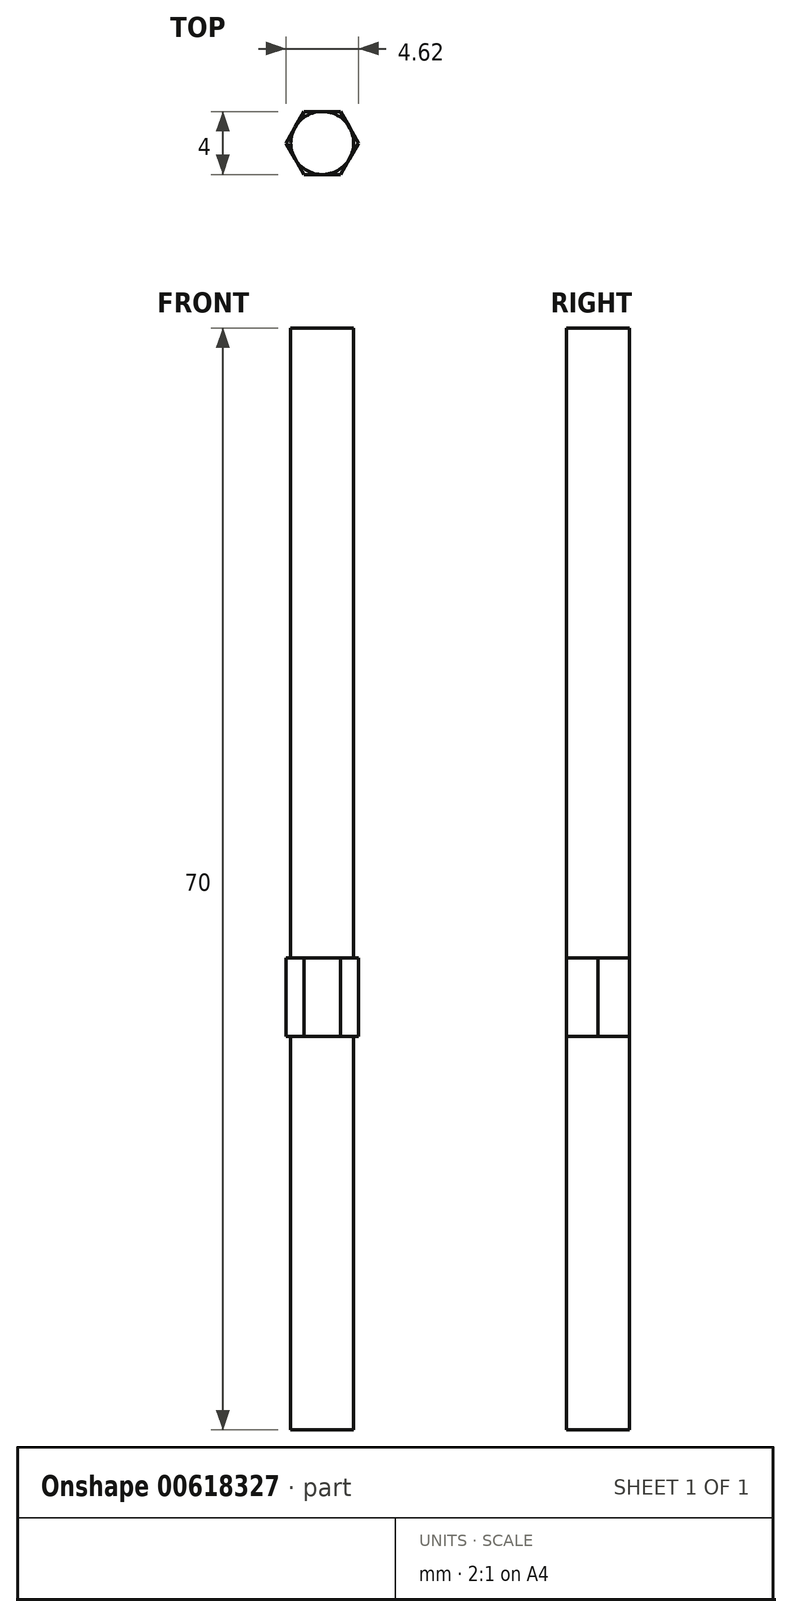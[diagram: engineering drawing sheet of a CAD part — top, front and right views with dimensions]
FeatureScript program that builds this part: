
annotation { "Feature Type Name" : "Feature", "Feature Type Description" : "" }
export const myFeature = defineFeature(function(context is Context, id is Id, definition is map)
    precondition{}
    {
        {
            var Q0;
            Q0=qCreatedBy(makeId("Top.planeOp"),FACE);
            var sketch = newSketch(context, id + "F0", { "sketchPlane" : qUnion([Q0])});
            skCircle(sketch, "E0", {"center": v(0, 0) * mm, "radius": 2 * mm});
            skSolve(sketch);
        }
        {
            var Q0;
            Q0=qSketchRegion(id+"F0",true);
            extrude(context, id + "F1", {"entities" : qUnion([Q0]), "depth" : 25 * mm, "offsetDistance" : 25 * mm});
        }
        {
            var Q0;
            Q0=makeQuery(id+"F1.opExtrude","CAP_FACE",FACE,{"disambiguationData":[OSD([sQuery(id+"F0.wireOp",EDGE,"E0")])],"isStart":false});
            var sketch = newSketch(context, id + "F2", { "sketchPlane" : qUnion([Q0])});
            skCircle(sketch, "E1.cCircle", {"center": v(0, 0) * mm, "radius": 2 * mm, "construction": true});
            skLineSegment(sketch, "E1.0", {"start": v(-1.15, 2) * mm, "end": v(1.15, 2) * mm});
            skLineSegment(sketch, "E1.1", {"start": v(1.15, 2) * mm, "end": v(2.3, 0) * mm});
            skLineSegment(sketch, "E1.2", {"start": v(2.3, 0) * mm, "end": v(1.15, -2) * mm});
            skLineSegment(sketch, "E1.3", {"start": v(1.15, -2) * mm, "end": v(-1.15, -2) * mm});
            skLineSegment(sketch, "E1.4", {"start": v(-1.15, -2) * mm, "end": v(-2.3, 0) * mm});
            skLineSegment(sketch, "E1.5", {"start": v(-2.3, 0) * mm, "end": v(-1.15, 2) * mm});
            skPoint(sketch, "E1.0.midPoint", {"position": v(0, 2) * mm});
            skSolve(sketch);
        }
        {
            var Q0;
            {var subQ0=sQuery(id+"F2.wireOp",EDGE,"E1.5");var subQ1=sQuery(id+"F2.wireOp",EDGE,"E1.0");var subQ2=makeQuery(id+"F2.imprint","INTERSECT",VERTEX,{"derivedFrom":[subQ1,subQ0]});Q0=makeQuery(id+"F2.imprint","IMPRINT",FACE,{"disambiguationData":[TD([[makeQuery(id+"F2.imprint","IMPRINT",EDGE,{"disambiguationData":[TD([[subQ2,-1.0]])],"derivedFrom":subQ1}),-1.0]])]});}
            var Q1;
            {var subQ0=sQuery(id+"F2.wireOp",EDGE,"E1.5");var subQ1=sQuery(id+"F2.wireOp",EDGE,"E1.4");var subQ2=makeQuery(id+"F2.imprint","INTERSECT",VERTEX,{"derivedFrom":[subQ1,subQ0]});Q1=makeQuery(id+"F2.imprint","IMPRINT",FACE,{"disambiguationData":[TD([[makeQuery(id+"F2.imprint","IMPRINT",EDGE,{"disambiguationData":[TD([[subQ2,1.0]])],"derivedFrom":subQ1}),-1.0]])]});}
            var Q2;
            {var subQ0=sQuery(id+"F2.wireOp",EDGE,"E1.4");var subQ1=sQuery(id+"F2.wireOp",EDGE,"E1.3");var subQ2=makeQuery(id+"F2.imprint","INTERSECT",VERTEX,{"derivedFrom":[subQ1,subQ0]});Q2=makeQuery(id+"F2.imprint","IMPRINT",FACE,{"disambiguationData":[TD([[makeQuery(id+"F2.imprint","IMPRINT",EDGE,{"disambiguationData":[TD([[subQ2,1.0]])],"derivedFrom":subQ1}),-1.0]])]});}
            var Q3;
            {var subQ0=sQuery(id+"F2.wireOp",EDGE,"E1.3");var subQ1=sQuery(id+"F2.wireOp",EDGE,"E1.2");var subQ2=makeQuery(id+"F2.imprint","INTERSECT",VERTEX,{"derivedFrom":[subQ1,subQ0]});Q3=makeQuery(id+"F2.imprint","IMPRINT",FACE,{"disambiguationData":[TD([[makeQuery(id+"F2.imprint","IMPRINT",EDGE,{"disambiguationData":[TD([[subQ2,1.0]])],"derivedFrom":subQ1}),-1.0]])]});}
            var Q4;
            {var subQ0=sQuery(id+"F2.wireOp",EDGE,"E1.2");var subQ1=sQuery(id+"F2.wireOp",EDGE,"E1.1");var subQ2=makeQuery(id+"F2.imprint","INTERSECT",VERTEX,{"derivedFrom":[subQ1,subQ0]});Q4=makeQuery(id+"F2.imprint","IMPRINT",FACE,{"disambiguationData":[TD([[makeQuery(id+"F2.imprint","IMPRINT",EDGE,{"disambiguationData":[TD([[subQ2,1.0]])],"derivedFrom":subQ1}),-1.0]])]});}
            var Q5;
            {var subQ0=sQuery(id+"F2.wireOp",EDGE,"E1.1");var subQ1=sQuery(id+"F2.wireOp",EDGE,"E1.0");var subQ2=makeQuery(id+"F2.imprint","INTERSECT",VERTEX,{"derivedFrom":[subQ1,subQ0]});Q5=makeQuery(id+"F2.imprint","IMPRINT",FACE,{"disambiguationData":[TD([[makeQuery(id+"F2.imprint","IMPRINT",EDGE,{"disambiguationData":[TD([[subQ2,1.0]])],"derivedFrom":subQ1}),-1.0]])]});}
            var Q6;
            {var subQ0=makeQuery(id+"F1.opExtrude","CAP_EDGE",EDGE,{"disambiguationData":[OSD([sQuery(id+"F0.wireOp",EDGE,"E0")])],"isStart":false});var subQ4=makeQuery(id+"F2.imprint","INTERSECT",VERTEX,{"derivedFrom":[subQ0,sQuery(id+"F2.wireOp",EDGE,"E1.0")]});Q6=makeQuery(id+"F2.imprint","IMPRINT",FACE,{"disambiguationData":[TD([[makeQuery(id+"F2.imprint","IMPRINT",EDGE,{"disambiguationData":[TD([[subQ4,1.0]])],"derivedFrom":subQ0}),1.0]])]});}
            extrude(context, id + "F3", {"entities" : qUnion([Q0, Q1, Q2, Q3, Q4, Q5, Q6]), "operationType" : NewBodyOperationType.ADD, "depth" : 5 * mm, "offsetDistance" : 25 * mm});
        }
        {
            var Q0;
            Q0=makeQuery(id+"F3.opExtrude","CAP_FACE",FACE,{"disambiguationData":[OSD([sQuery(id+"F2.wireOp",EDGE,"E1.0"),sQuery(id+"F2.wireOp",EDGE,"E1.1"),sQuery(id+"F2.wireOp",EDGE,"E1.2"),sQuery(id+"F2.wireOp",EDGE,"E1.3"),sQuery(id+"F2.wireOp",EDGE,"E1.4"),sQuery(id+"F2.wireOp",EDGE,"E1.5")])],"isStart":false});
            var sketch = newSketch(context, id + "F4", { "sketchPlane" : qUnion([Q0])});
            skCircle(sketch, "E2", {"center": v(0, 0) * mm, "radius": 2 * mm});
            skSolve(sketch);
        }
        {
            var Q0;
            {var subQ0=sQuery(id+"F4.wireOp",EDGE,"E2");var subQ4=makeQuery(id+"F4.imprint","INTERSECT",VERTEX,{"derivedFrom":[makeQuery(id+"F3.opExtrude","CAP_EDGE",EDGE,{"disambiguationData":[OSD([sQuery(id+"F2.wireOp",EDGE,"E1.0")])],"isStart":false}),subQ0]});Q0=makeQuery(id+"F4.imprint","IMPRINT",FACE,{"disambiguationData":[TD([[makeQuery(id+"F4.imprint","IMPRINT",EDGE,{"disambiguationData":[TD([[subQ4,1.0]])],"derivedFrom":subQ0}),1.0]])]});}
            extrude(context, id + "F5", {"entities" : qUnion([Q0]), "operationType" : NewBodyOperationType.ADD, "depth" : 40 * mm, "offsetDistance" : 25 * mm});
        }
    });
